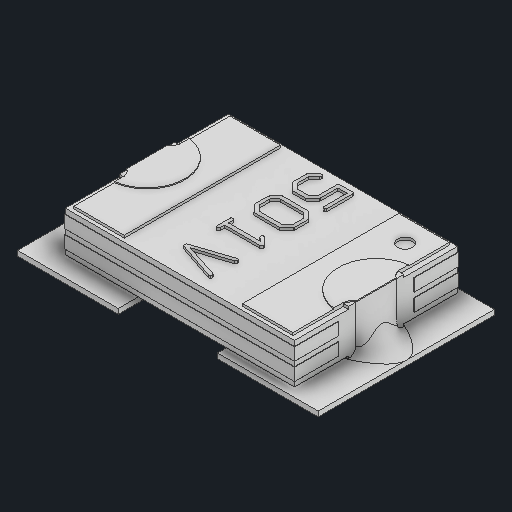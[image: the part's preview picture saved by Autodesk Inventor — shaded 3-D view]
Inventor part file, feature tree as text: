
AUTODESK INVENTOR PART (.ipt)
format: ipt  version: 2023 (Build 270158000, 158)  size: 378,368 bytes
history: native  units: in
note: dims shown in document units (in); Inventor stores cm internally (conversion verified against a paired STEP export)
features: mirror x1
ambient origin geometry x8: Origin, YZ Plane, XZ Plane, XY Plane, X Axis, Y Axis, Z Axis, Center Point
bodies: Solid1 (feature_tree)
feature tree (1):
  mirror  "Mirror5"
